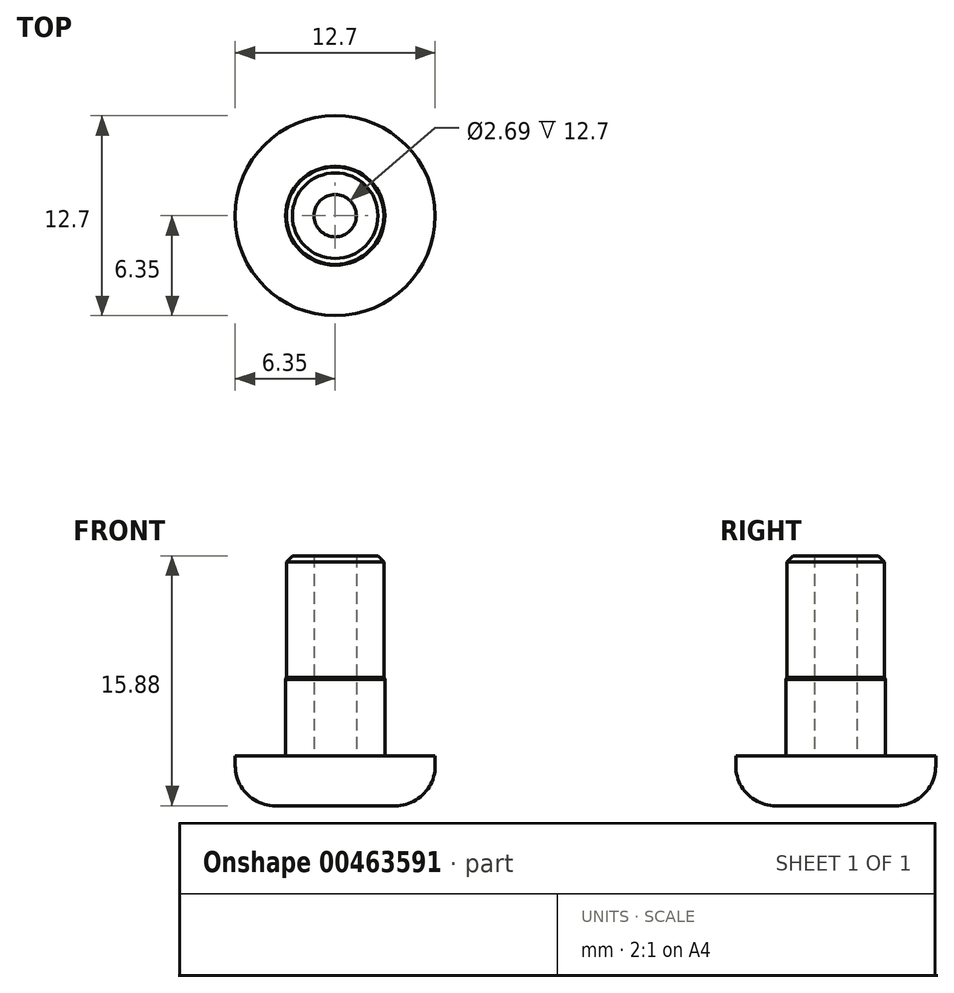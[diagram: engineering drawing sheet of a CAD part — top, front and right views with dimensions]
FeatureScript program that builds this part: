
annotation { "Feature Type Name" : "Feature", "Feature Type Description" : "" }
export const myFeature = defineFeature(function(context is Context, id is Id, definition is map)
    precondition{}
    {
        {
            var Q0;
            Q0=qCreatedBy(makeId("Front.planeOp"),FACE);
            var sketch = newSketch(context, id + "F0", { "sketchPlane" : qUnion([Q0])});
            skLineSegment(sketch, "E0", {"start": v(0, 0) * mm, "end": v(6.35, 0) * mm});
            skLineSegment(sketch, "E1", {"start": v(6.35, 0) * mm, "end": v(6.35, 3.18) * mm});
            skLineSegment(sketch, "E2", {"start": v(0, 0) * mm, "end": v(0, 3.18) * mm});
            skLineSegment(sketch, "E3", {"start": v(6.35, 3.18) * mm, "end": v(3.15, 3.18) * mm});
            skLineSegment(sketch, "E4", {"start": v(3.1, 8) * mm, "end": v(3.1, 15.88) * mm});
            skPoint(sketch, "E5", {"position": v(0, 15.88) * mm});
            skLineSegment(sketch, "E6", {"start": v(3.1, 15.88) * mm, "end": v(1.35, 15.88) * mm});
            skLineSegment(sketch, "E7", {"start": v(3.15, 3.18) * mm, "end": v(3.15, 8) * mm});
            skLineSegment(sketch, "E8", {"start": v(3.15, 8) * mm, "end": v(3.1, 8) * mm});
            skLineSegment(sketch, "E9", {"start": v(1.35, 15.88) * mm, "end": v(1.35, 3.18) * mm});
            skLineSegment(sketch, "E10", {"start": v(1.35, 3.18) * mm, "end": v(0, 3.18) * mm});
            skSolve(sketch);
        }
        {
            var Q0;
            Q0=makeQuery(id+"F0.imprint","IMPRINT",FACE,{"disambiguationData":[TD([[makeQuery(id+"F0.imprint","IMPRINT",EDGE,{"derivedFrom":sQuery(id+"F0.wireOp",EDGE,"E0")}),1.0]])]});
            var Q1;
            Q1=sQuery(id+"F0.wireOp",EDGE,"E2");
            revolve(context, id + "F1", {"entities" : qUnion([Q0]), "axis" : qUnion([Q1]), "revolveType" : RevolveType.FULL});
        }
        {
            var Q0;
            Q0=makeQuery(id+"F1.opRevolve","SWEPT_EDGE",EDGE,{"disambiguationData":[OSD([sQuery(id+"F0.wireOp",EDGE,"E0"),sQuery(id+"F0.wireOp",EDGE,"E1")])]});
            fillet(context, id + "F2", {"entities" : qUnion([Q0]), "radius" : 2.54 * mm, "tangentPropagation" : true, "allowEdgeOverflow" : false});
        }
        {
            var Q0;
            Q0=makeQuery(id+"F1.opRevolve","SWEPT_EDGE",EDGE,{"disambiguationData":[OSD([sQuery(id+"F0.wireOp",EDGE,"E7"),sQuery(id+"F0.wireOp",EDGE,"E8")])]});
            chamfer(context, id + "F3", {"entities" : qUnion([Q0]), "width" : 0.05 * mm, "tangentPropagation" : true});
        }
        {
            var Q0;
            Q0=makeQuery(id+"F1.opRevolve","SWEPT_FACE",FACE,{"disambiguationData":[OSD([sQuery(id+"F0.wireOp",EDGE,"E4")])]});
            chamfer(context, id + "F4", {"entities" : qUnion([Q0]), "width" : 0.38 * mm, "tangentPropagation" : true});
        }
    });
